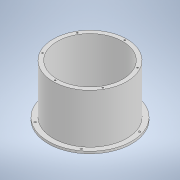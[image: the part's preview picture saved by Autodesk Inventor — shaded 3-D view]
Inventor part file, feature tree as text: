
AUTODESK INVENTOR PART (.ipt)
format: ipt  version: 2020 (Build 240168000, 168)  size: 162,304 bytes
history: native  units: mm
features: sketch x3, hole x2, projected_geometry x2, revolve x1, pattern_circular x1
ambient origin geometry x8: Origin, YZ Plane, XZ Plane, XY Plane, X Axis, Y Axis, Z Axis, Center Point
bodies: Body1 (feature_tree)
feature tree (9):
  revolve  "Revolution1"  [1 undecoded]
  hole  "Hole1"  [1 undecoded]
  pattern_circular  "Circular Pattern1"  Angle=90.0deg  [1 undecoded]
  hole  "Hole2"  [1 undecoded]
  sketch  "Sketch2"  dims[d4=5.0mm d5=11.0mm]
  sketch  "Sketch3"  dims[d6=9.0mm d8=110.0mm]
  projected_geometry  "Projected Loop1"
  sketch  "Sketch5"  dims[d9=4.0mm d10=90.0deg d11=5.5mm d12=5.5mm d13=4.5mm d14=7.0mm d15=9.4mm d16=2.0mm d17=90.0deg d18=8.0mm d19=20.594885mm d20=50.0mm d21=360.0deg d38=81.5mm d39=4.5mm d40=4.5mm d41=60.0mm d43=360.0deg d45=3.242mm d46=10.0mm d47=6.3mm d48=2.0mm d49=90.0deg d50=13.0mm d51=20.594885mm]
  projected_geometry  "Projected Loop3"
note: 4 required parameter values undecoded (feature->parameter linkage not recoverable at this tier; creation-order binding heuristic only, values carry confidence <= 0.55)